# Revit family: 75005
name_source: partatom
category: Doors
revit_build: Autodesk Revit 2018 (Build: 20170223_1515(x64)
units: mm (PartAtom-declared; Revit-internal decimal feet)

## family parameters
Always vertical = Yes
Cut with Voids When Loaded = No
Host = Wall
OmniClass Number = 23.30.10.17.11
OmniClass Title = Sliding Doors
Room Calculation Point = No
Shared = No

## types (4) — shared parameters
04 CSI = 08 41 13
95 CSI = 8411
Analytic Construction = <None>
Cost Info = https://www.nanawall.com
Description = Single Track Sliding System
Detail Component in Plan = Yes
Detail Component in Section = Yes
Engineering Details URL = https://www.nanawall.com
Exterior Wall Offset = 4"
Glass Material = Glass - NanaWall - Generic
Glazing Options = https://www.nanawall.com
Glazing Thickness = 241/256"
Height = 9' - 0"
Height Constraint = 9' - 0"
Installation and Service URL = https://www.nanawall.com
Jamb Height = 9' - 0 61/64"
Manufacturer = NanaWall Systems, Inc.
Manufacturer Fax = (415) 383-0312
Model = HSW60 - Concept H
NanaWall Configurator = http://www.nanawall.com
Opening Width = 9' - 6 97/128"
Performance URL = https://www.nanawall.com
Product Page URL = https://www.nanawall.com
Rough Height = 9' - 0"
Rough Width = 9' - 10 7/64"
Sash = Metal - NanaWall - Aluminum
Sills Available = Surface Mounted, Floor Sockets, Low Profile Saddle, Flush
Size Note = Adjust Height and Width as necessary to fit your project needs. Multiple Panel and opening configurations are available. See Product Page URL for more information.
Subcategory = Sliding Glass Wall
Surface Mounted Sill = No
Thickness = 2 1/2"
URL = http://www.nanawall.com
Wall Closure = By host
Warranty URL = http://www.nanawall.com
Width = 10' - 0"
Width C = 10' - 0"
not DIP = No

## per-type parameters (varying)
| type | Assembly Code | Flush Sill | Low Profile Saddle Sill | No Sill - Floor Socket |
| HSW60-Configuration_H Surface Mounted Sill | B2050.4010 | No | Yes | No |
| HSW60-Configuration_H Low Profile Saddle Sill | B2050.1040 | No | Yes | No |
| HSW60-Configuration_H Flush Sill | B2050.1040 | Yes | No | No |
| HSW60-Configuration_H No Sill - Floor Sockets | B2050.1040 | No | No | Yes |

## geometry (parser evidence)
native form markers: Blend x1700, Sweep x49
no freeform markers — native parametric forms only
